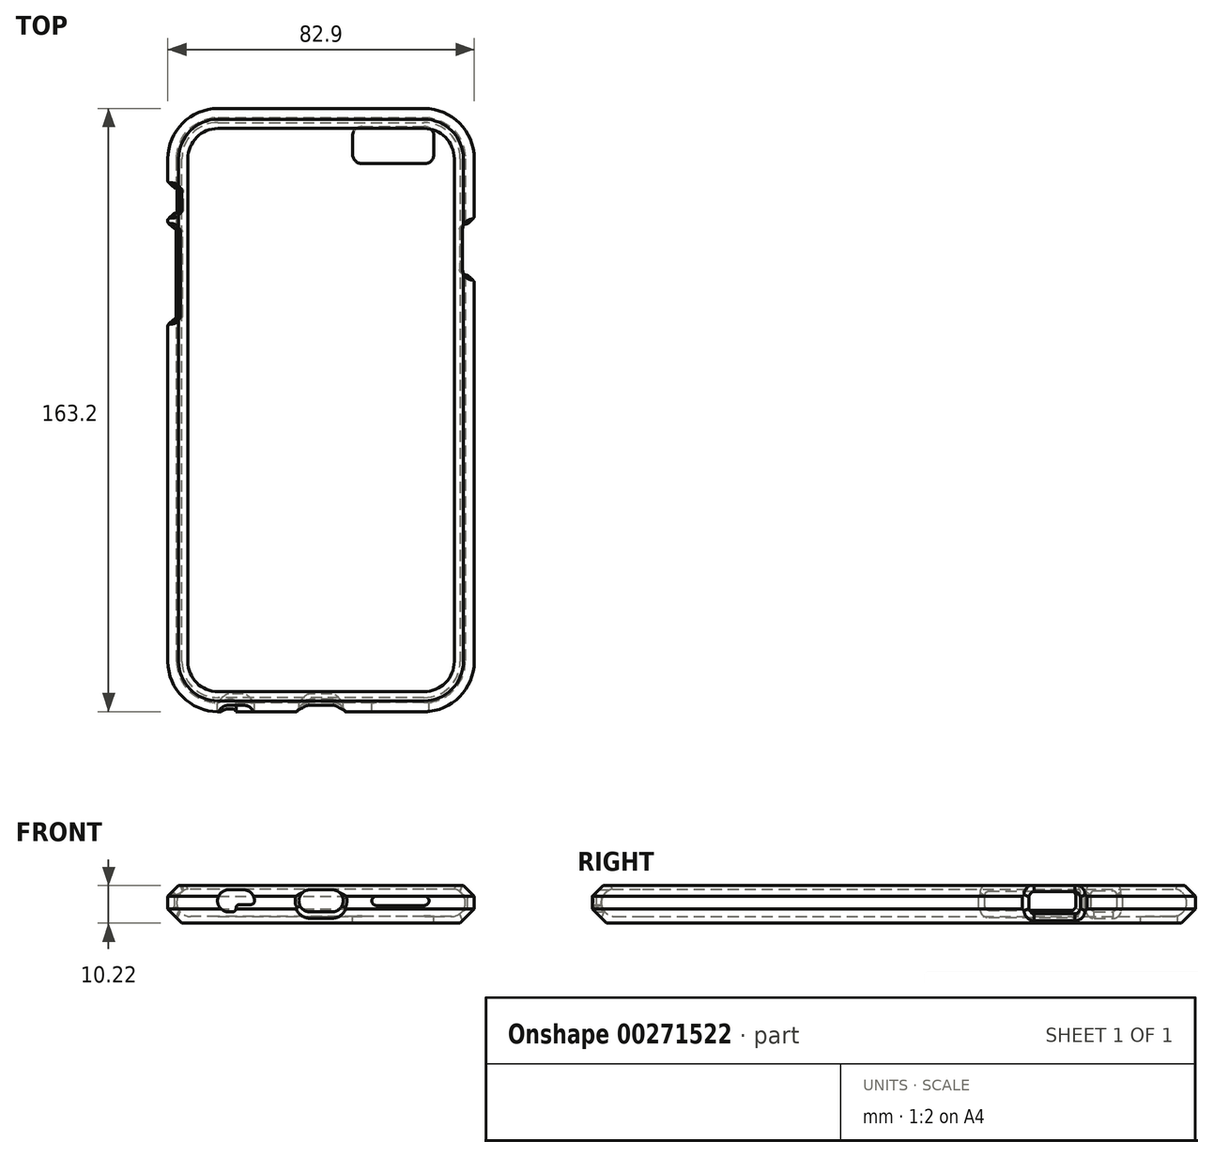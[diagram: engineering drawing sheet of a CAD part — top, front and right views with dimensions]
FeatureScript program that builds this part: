
annotation { "Feature Type Name" : "Feature", "Feature Type Description" : "" }
export const myFeature = defineFeature(function(context is Context, id is Id, definition is map)
    precondition{}
    {
        {
            assignVariable(context, id + "F0", {"name" : "HoleChamferLength", "anyValue" : 1.25});
        }
        {
            assignVariable(context, id + "F1", {"name" : "HoleChamferTopBottom", "anyValue" : 1.75});
        }
        {
            var Q0;
            Q0=qCreatedBy(makeId("Top.planeOp"),FACE);
            var sketch = newSketch(context, id + "F2", { "sketchPlane" : qUnion([Q0])});
            skLineSegment(sketch, "E0.bottom", {"start": v(27.85, 79.2) * mm, "end": v(0, 79.2) * mm});
            skLineSegment(sketch, "E0.top", {"start": v(27.85, -79.2) * mm, "end": v(-27.85, -79.2) * mm});
            skLineSegment(sketch, "E0.left", {"start": v(39.05, 68) * mm, "end": v(39.05, -68) * mm});
            skLineSegment(sketch, "E0.right", {"start": v(-39.05, 68) * mm, "end": v(-39.05, -68) * mm});
            skPoint(sketch, "E0.middle", {"position": v(0, 0) * mm});
            skPoint(sketch, "E1.visualSharp", {"position": v(-39.05, 79.2) * mm});
            skArc(sketch, "E1.filletArc", {"start": v(-27.85, 79.2) * mm, "mid": v(-35.77, 75.92) * mm, "end": v(-39.05, 68) * mm});
            skPoint(sketch, "E2.visualSharp", {"position": v(39.05, 79.2) * mm});
            skArc(sketch, "E2.filletArc", {"start": v(39.05, 68) * mm, "mid": v(35.77, 75.92) * mm, "end": v(27.85, 79.2) * mm});
            skPoint(sketch, "E3.visualSharp", {"position": v(39.05, -79.2) * mm});
            skArc(sketch, "E3.filletArc", {"start": v(27.85, -79.2) * mm, "mid": v(35.77, -75.92) * mm, "end": v(39.05, -68) * mm});
            skPoint(sketch, "E4.visualSharp", {"position": v(-39.05, -79.2) * mm});
            skArc(sketch, "E4.filletArc", {"start": v(-39.05, -68) * mm, "mid": v(-35.77, -75.92) * mm, "end": v(-27.85, -79.2) * mm});
            skLineSegment(sketch, "E5", {"start": v(0, 79.2) * mm, "end": v(-27.85, 79.2) * mm});
            skSolve(sketch);
        }
        {
            var Q0;
            Q0=qCreatedBy(makeId("Right.planeOp"),FACE);
            var sketch = newSketch(context, id + "F3", { "sketchPlane" : qUnion([Q0])});
            skPoint(sketch, "E6.0", {"position": v(79.2, 0) * mm});
            skArc(sketch, "E7", {"start": v(75.45, -3.75) * mm, "mid": v(79.2, 0) * mm, "end": v(75.45, 3.75) * mm});
            skLineSegment(sketch, "E8", {"start": v(75.45, -3.75) * mm, "end": v(75.45, 3.75) * mm, "construction": true});
            skLineSegment(sketch, "E9", {"start": v(81.6, -1.75) * mm, "end": v(81.6, 1.75) * mm});
            skLineSegment(sketch, "E10", {"start": v(81.6, 1.75) * mm, "end": v(79.85, 3.5) * mm});
            skLineSegment(sketch, "E11.trimOffspring", {"start": v(79.85, -3.5) * mm, "end": v(81.6, -1.75) * mm});
            skLineSegment(sketch, "E12", {"start": v(75.45, -5.55) * mm, "end": v(75.45, -3.75) * mm});
            skLineSegment(sketch, "E13", {"start": v(75.45, -5.55) * mm, "end": v(84.8, -5.55) * mm, "construction": true});
            skPoint(sketch, "E14", {"position": v(81.6, 0) * mm});
            skPoint(sketch, "E15.visualSharp", {"position": v(66.64, 4.7) * mm});
            skArc(sketch, "E15.filletArc", {"start": v(77.42, 4.67) * mm, "mid": v(76.63, 4.4) * mm, "end": v(76.2, 3.67) * mm});
            skLineSegment(sketch, "E16", {"start": v(79.85, -3.5) * mm, "end": v(77.8, -5.55) * mm});
            skLineSegment(sketch, "E17", {"start": v(77.8, -5.55) * mm, "end": v(75.45, -5.55) * mm});
            skLineSegment(sketch, "E18", {"start": v(79.85, 3.5) * mm, "end": v(78.68, 4.67) * mm});
            skLineSegment(sketch, "E19", {"start": v(78.68, 4.67) * mm, "end": v(77.42, 4.67) * mm});
            skLineSegment(sketch, "E20", {"start": v(76.2, 3.67) * mm, "end": v(66.74, 5.6) * mm, "construction": true});
            skSolve(sketch);
        }
        {
            var Q0;
            Q0=sQuery(id+"F2.wireOp",EDGE,"E5");
            var Q1;
            Q1=sQuery(id+"F2.wireOp",VERTEX,"E5.end");
            cPlane(context, id + "F4", {"entities" : qUnion([Q0, Q1]), "cplaneType" : CPlaneType.LINE_POINT, "offset" : 25 * mm, "width" : 150 * mm, "height" : 150 * mm});
        }
        {
            var Q0;
            Q0=sQuery(id+"F2.wireOp",EDGE,"E0.bottom");
            var Q1;
            Q1=sQuery(id+"F2.wireOp",VERTEX,"E2.filletArc.end");
            cPlane(context, id + "F5", {"entities" : qUnion([Q0, Q1]), "cplaneType" : CPlaneType.LINE_POINT, "offset" : 25 * mm, "width" : 150 * mm, "height" : 150 * mm});
        }
        {
            var Q0;
            Q0=sQuery(id+"F2.wireOp",EDGE,"E0.right");
            var Q1;
            Q1=sQuery(id+"F2.wireOp",VERTEX,"E0.right.end");
            cPlane(context, id + "F6", {"entities" : qUnion([Q0, Q1]), "cplaneType" : CPlaneType.LINE_POINT, "offset" : 25 * mm, "width" : 150 * mm, "height" : 150 * mm});
        }
        {
            var Q0;
            Q0=qCreatedBy(id+"F4.planeOp",FACE);
            var sketch = newSketch(context, id + "F7", { "sketchPlane" : qUnion([Q0])});
            skLineSegment(sketch, "E21.bottom", {"start": v(-25.55, -1.88) * mm, "end": v(-48.2, -1.88) * mm});
            skLineSegment(sketch, "E21.top", {"start": v(-25.55, 2.87) * mm, "end": v(-48.2, 2.87) * mm});
            skLineSegment(sketch, "E21.left", {"start": v(-24.55, -0.88) * mm, "end": v(-24.55, 1.87) * mm});
            skLineSegment(sketch, "E21.right", {"start": v(-49.2, -0.88) * mm, "end": v(-49.2, 1.87) * mm});
            skPoint(sketch, "E21.middle", {"position": v(-36.87, 0.5) * mm});
            skPoint(sketch, "E22.visualSharp", {"position": v(-49.2, 2.87) * mm});
            skArc(sketch, "E22.filletArc", {"start": v(-48.2, 2.87) * mm, "mid": v(-48.9, 2.58) * mm, "end": v(-49.2, 1.87) * mm});
            skPoint(sketch, "E23.visualSharp", {"position": v(-49.2, -1.88) * mm});
            skArc(sketch, "E23.filletArc", {"start": v(-49.2, -0.88) * mm, "mid": v(-48.9, -1.58) * mm, "end": v(-48.2, -1.88) * mm});
            skPoint(sketch, "E24.visualSharp", {"position": v(-24.55, 2.87) * mm});
            skArc(sketch, "E24.filletArc", {"start": v(-24.55, 1.87) * mm, "mid": v(-24.84, 2.58) * mm, "end": v(-25.55, 2.87) * mm});
            skPoint(sketch, "E25.visualSharp", {"position": v(-24.55, -1.88) * mm});
            skArc(sketch, "E25.filletArc", {"start": v(-25.55, -1.88) * mm, "mid": v(-24.84, -1.58) * mm, "end": v(-24.55, -0.88) * mm});
            skLineSegment(sketch, "E26.bottom", {"start": v(-59.2, 3.12) * mm, "end": v(-54.2, 3.12) * mm});
            skLineSegment(sketch, "E26.top", {"start": v(-59.2, -2.13) * mm, "end": v(-54.2, -2.13) * mm});
            skLineSegment(sketch, "E26.left", {"start": v(-60.2, 2.12) * mm, "end": v(-60.2, -1.13) * mm});
            skLineSegment(sketch, "E26.right", {"start": v(-53.2, 2.12) * mm, "end": v(-53.2, -1.13) * mm});
            skPoint(sketch, "E26.middle", {"position": v(-56.7, 0.5) * mm});
            skPoint(sketch, "E27.visualSharp", {"position": v(-60.2, 3.12) * mm});
            skArc(sketch, "E27.filletArc", {"start": v(-59.2, 3.12) * mm, "mid": v(-59.9, 2.83) * mm, "end": v(-60.2, 2.12) * mm});
            skPoint(sketch, "E28.visualSharp", {"position": v(-60.2, -2.13) * mm});
            skArc(sketch, "E28.filletArc", {"start": v(-60.2, -1.13) * mm, "mid": v(-59.9, -1.83) * mm, "end": v(-59.2, -2.13) * mm});
            skPoint(sketch, "E29.visualSharp", {"position": v(-53.2, -2.13) * mm});
            skArc(sketch, "E29.filletArc", {"start": v(-54.2, -2.13) * mm, "mid": v(-53.5, -1.83) * mm, "end": v(-53.2, -1.13) * mm});
            skPoint(sketch, "E30.visualSharp", {"position": v(-53.2, 3.12) * mm});
            skArc(sketch, "E30.filletArc", {"start": v(-53.2, 2.12) * mm, "mid": v(-53.5, 2.83) * mm, "end": v(-54.2, 3.12) * mm});
            skSolve(sketch);
        }
        {
            var Q0;
            Q0=qCreatedBy(id+"F5.planeOp",FACE);
            var sketch = newSketch(context, id + "F8", { "sketchPlane" : qUnion([Q0])});
            skLineSegment(sketch, "E31.bottom", {"start": v(-48.95, 2.75) * mm, "end": v(-37.95, 2.75) * mm});
            skLineSegment(sketch, "E31.top", {"start": v(-48.95, -2.75) * mm, "end": v(-37.95, -2.75) * mm});
            skLineSegment(sketch, "E31.left", {"start": v(-50.45, 1.25) * mm, "end": v(-50.45, -1.25) * mm});
            skLineSegment(sketch, "E31.right", {"start": v(-36.45, 1.25) * mm, "end": v(-36.45, -1.25) * mm});
            skPoint(sketch, "E31.middle", {"position": v(-43.45, 0) * mm});
            skPoint(sketch, "E32.visualSharp", {"position": v(-50.45, 2.75) * mm});
            skArc(sketch, "E32.filletArc", {"start": v(-48.95, 2.75) * mm, "mid": v(-50.01, 2.31) * mm, "end": v(-50.45, 1.25) * mm});
            skPoint(sketch, "E33.visualSharp", {"position": v(-50.45, -2.75) * mm});
            skArc(sketch, "E33.filletArc", {"start": v(-50.45, -1.25) * mm, "mid": v(-50.01, -2.31) * mm, "end": v(-48.95, -2.75) * mm});
            skPoint(sketch, "E34.visualSharp", {"position": v(-36.45, -2.75) * mm});
            skArc(sketch, "E34.filletArc", {"start": v(-37.95, -2.75) * mm, "mid": v(-36.89, -2.31) * mm, "end": v(-36.45, -1.25) * mm});
            skPoint(sketch, "E35.visualSharp", {"position": v(-36.45, 2.75) * mm});
            skArc(sketch, "E35.filletArc", {"start": v(-36.45, 1.25) * mm, "mid": v(-36.89, 2.31) * mm, "end": v(-37.95, 2.75) * mm});
            skSolve(sketch);
        }
        {
            var Q0;
            Q0=qCreatedBy(id+"F6.planeOp",FACE);
            var sketch = newSketch(context, id + "F9", { "sketchPlane" : qUnion([Q0])});
            skLineSegment(sketch, "E36.bottom", {"start": v(3, 3.5) * mm, "end": v(-3, 3.5) * mm});
            skLineSegment(sketch, "E36.top", {"start": v(3, -2.5) * mm, "end": v(-3, -2.5) * mm});
            skLineSegment(sketch, "E36.left", {"start": v(6, 0.5) * mm, "end": v(6, 0.5) * mm});
            skLineSegment(sketch, "E36.right", {"start": v(-6, 0.5) * mm, "end": v(-6, 0.5) * mm});
            skPoint(sketch, "E36.middle", {"position": v(0, 0.5) * mm});
            skArc(sketch, "E37", {"start": v(-25, 3.5) * mm, "mid": v(-28, 0.5) * mm, "end": v(-25, -2.5) * mm});
            skPoint(sketch, "E38.visualSharp", {"position": v(-6, 3.5) * mm});
            skArc(sketch, "E38.filletArc", {"start": v(-3, 3.5) * mm, "mid": v(-5.12, 2.62) * mm, "end": v(-6, 0.5) * mm});
            skPoint(sketch, "E39.visualSharp", {"position": v(-6, -2.5) * mm});
            skArc(sketch, "E39.filletArc", {"start": v(-6, 0.5) * mm, "mid": v(-5.12, -1.62) * mm, "end": v(-3, -2.5) * mm});
            skPoint(sketch, "E40.visualSharp", {"position": v(6, -2.5) * mm});
            skArc(sketch, "E40.filletArc", {"start": v(3, -2.5) * mm, "mid": v(5.12, -1.62) * mm, "end": v(6, 0.5) * mm});
            skPoint(sketch, "E41.visualSharp", {"position": v(6, 3.5) * mm});
            skArc(sketch, "E41.filletArc", {"start": v(6, 0.5) * mm, "mid": v(5.12, 2.62) * mm, "end": v(3, 3.5) * mm});
            skArc(sketch, "E42", {"start": v(-21, -2.5) * mm, "mid": v(-19.27, -1.95) * mm, "end": v(-18.17, -0.5) * mm, "construction": true});
            skLineSegment(sketch, "E43", {"start": v(-21, 3.5) * mm, "end": v(-25, 3.5) * mm});
            skLineSegment(sketch, "E44", {"start": v(-21, -2.5) * mm, "end": v(-23, -2.5) * mm, "construction": true});
            skLineSegment(sketch, "E45", {"start": v(15, 0.5) * mm, "end": v(28, 0.5) * mm, "construction": true});
            skArc(sketch, "E46.0.startCap", {"start": v(15, -0.75) * mm, "mid": v(13.75, 0.5) * mm, "end": v(15, 1.75) * mm});
            skArc(sketch, "E46.0.endCap", {"start": v(28, 1.75) * mm, "mid": v(29.25, 0.5) * mm, "end": v(28, -0.75) * mm});
            skLineSegment(sketch, "E46.0.left", {"start": v(15, 1.75) * mm, "end": v(28, 1.75) * mm});
            skLineSegment(sketch, "E46.0.right", {"start": v(15, -0.75) * mm, "end": v(28, -0.75) * mm});
            skLineSegment(sketch, "E47", {"start": v(-23, -1.5) * mm, "end": v(-23, -1.5) * mm});
            skLineSegment(sketch, "E48", {"start": v(-22, -0.5) * mm, "end": v(-19, -0.5) * mm});
            skLineSegment(sketch, "E49", {"start": v(-24, -2.5) * mm, "end": v(-25, -2.5) * mm});
            skArc(sketch, "E50", {"start": v(-18, 0.5) * mm, "mid": v(-18.88, 2.62) * mm, "end": v(-21, 3.5) * mm});
            skPoint(sketch, "E51.visualSharp", {"position": v(-23, -0.5) * mm});
            skArc(sketch, "E51.filletArc", {"start": v(-22, -0.5) * mm, "mid": v(-22.7, -0.8) * mm, "end": v(-23, -1.5) * mm});
            skPoint(sketch, "E52.visualSharp", {"position": v(-23, -2.5) * mm});
            skArc(sketch, "E52.filletArc", {"start": v(-24, -2.5) * mm, "mid": v(-23.3, -2.2) * mm, "end": v(-23, -1.5) * mm});
            skPoint(sketch, "E53.visualSharp", {"position": v(-18.17, -0.5) * mm});
            skArc(sketch, "E53.filletArc", {"start": v(-19, -0.5) * mm, "mid": v(-18.3, -0.2) * mm, "end": v(-18, 0.5) * mm});
            skCircle(sketch, "E54", {"center": v(-25, 0.5) * mm, "radius": 2.5 * mm, "construction": true});
            skSolve(sketch);
        }
        {
            var Q0;
            Q0=qCreatedBy(makeId("Top.planeOp"),FACE);
            var sketch = newSketch(context, id + "F10", { "sketchPlane" : qUnion([Q0])});
            skLineSegment(sketch, "E55.bottom", {"start": v(28.05, 66.7) * mm, "end": v(11.05, 66.7) * mm});
            skLineSegment(sketch, "E55.top", {"start": v(28.05, 76.7) * mm, "end": v(11.05, 76.7) * mm});
            skLineSegment(sketch, "E55.left", {"start": v(30.55, 69.2) * mm, "end": v(30.55, 74.2) * mm});
            skLineSegment(sketch, "E55.right", {"start": v(8.55, 69.2) * mm, "end": v(8.55, 74.2) * mm});
            skPoint(sketch, "E55.middle", {"position": v(19.55, 71.7) * mm});
            skPoint(sketch, "E56.visualSharp", {"position": v(8.55, 76.7) * mm});
            skArc(sketch, "E56.filletArc", {"start": v(11.05, 76.7) * mm, "mid": v(9.28, 75.97) * mm, "end": v(8.55, 74.2) * mm});
            skPoint(sketch, "E57.visualSharp", {"position": v(8.55, 66.7) * mm});
            skArc(sketch, "E57.filletArc", {"start": v(8.55, 69.2) * mm, "mid": v(9.28, 67.43) * mm, "end": v(11.05, 66.7) * mm});
            skPoint(sketch, "E58.visualSharp", {"position": v(30.55, 66.7) * mm});
            skArc(sketch, "E58.filletArc", {"start": v(28.05, 66.7) * mm, "mid": v(29.82, 67.43) * mm, "end": v(30.55, 69.2) * mm});
            skPoint(sketch, "E59.visualSharp", {"position": v(30.55, 76.7) * mm});
            skArc(sketch, "E59.filletArc", {"start": v(30.55, 74.2) * mm, "mid": v(29.82, 75.97) * mm, "end": v(28.05, 76.7) * mm});
            skSolve(sketch);
        }
        {
            var Q0;
            Q0=qSketchRegion(id+"F3",true);
            var Q1;
            Q1=sQuery(id+"F2.wireOp",EDGE,"E5");
            var Q2;
            Q2=sQuery(id+"F2.wireOp",EDGE,"E1.filletArc");
            var Q3;
            Q3=sQuery(id+"F2.wireOp",EDGE,"E0.right");
            var Q4;
            Q4=sQuery(id+"F2.wireOp",EDGE,"E4.filletArc");
            var Q5;
            Q5=sQuery(id+"F2.wireOp",EDGE,"E0.top");
            var Q6;
            Q6=sQuery(id+"F2.wireOp",EDGE,"E3.filletArc");
            var Q7;
            Q7=sQuery(id+"F2.wireOp",EDGE,"E0.left");
            var Q8;
            Q8=sQuery(id+"F2.wireOp",EDGE,"E2.filletArc");
            var Q9;
            Q9=sQuery(id+"F2.wireOp",EDGE,"E0.bottom");
            sweep(context, id + "F11", {"profiles" : qUnion([Q0]), "path" : qUnion([Q1, Q2, Q3, Q4, Q5, Q6, Q7, Q8, Q9])});
        }
        {
            var Q0;
            Q0=qCreatedBy(makeId("Front.planeOp"),FACE);
            var sketch = newSketch(context, id + "F12", { "sketchPlane" : qUnion([Q0])});
            skLineSegment(sketch, "E60.0.0", {"start": v(35.3, -5.55) * mm, "end": v(27.85, -5.55) * mm});
            skLineSegment(sketch, "E60.0.1", {"start": v(27.85, -3.75) * mm, "end": v(27.85, -5.55) * mm});
            skLineSegment(sketch, "E60.0.2", {"start": v(27.85, -3.75) * mm, "end": v(35.3, -3.75) * mm});
            skLineSegment(sketch, "E60.0.3", {"start": v(35.3, -3.75) * mm, "end": v(35.3, -5.55) * mm});
            skLineSegment(sketch, "E60.1.0", {"start": v(27.85, -5.55) * mm, "end": v(-27.85, -5.55) * mm});
            skLineSegment(sketch, "E60.1.1", {"start": v(-27.85, -3.75) * mm, "end": v(-27.85, -5.55) * mm});
            skLineSegment(sketch, "E60.1.2", {"start": v(-27.85, -3.75) * mm, "end": v(27.85, -3.75) * mm});
            skLineSegment(sketch, "E60.1.3", {"start": v(27.85, -3.75) * mm, "end": v(27.85, -5.55) * mm});
            skLineSegment(sketch, "E60.2.0", {"start": v(-27.85, -5.55) * mm, "end": v(-35.3, -5.55) * mm});
            skLineSegment(sketch, "E60.2.1", {"start": v(-35.3, -3.75) * mm, "end": v(-35.3, -5.55) * mm});
            skLineSegment(sketch, "E60.2.2", {"start": v(-35.3, -3.75) * mm, "end": v(-27.85, -3.75) * mm});
            skLineSegment(sketch, "E60.2.3", {"start": v(-27.85, -3.75) * mm, "end": v(-27.85, -5.55) * mm});
            skSolve(sketch);
        }
        {
            var Q0;
            Q0=qSketchRegion(id+"F12",true);
            extrude(context, id + "F13", {"entities" : qUnion([Q0]), "operationType" : NewBodyOperationType.ADD, "endBound" : BoundingType.UP_TO_NEXT, "depth" : 25 * mm, "hasSecondDirection" : true, "secondDirectionBound" : SecondDirectionBoundingType.UP_TO_NEXT, "secondDirectionOppositeDirection" : true, "secondDirectionDepth" : 25 * mm});
        }
        {
            var Q0;
            Q0=qSketchRegion(id+"F7",true);
            extrude(context, id + "F14", {"entities" : qUnion([Q0]), "operationType" : NewBodyOperationType.REMOVE, "endBound" : BoundingType.THROUGH_ALL, "depth" : 25 * mm});
        }
        {
            var Q0;
            Q0=qSketchRegion(id+"F8",true);
            extrude(context, id + "F15", {"entities" : qUnion([Q0]), "operationType" : NewBodyOperationType.REMOVE, "endBound" : BoundingType.THROUGH_ALL, "oppositeDirection" : true, "depth" : 25 * mm});
        }
        {
            var Q0;
            Q0=makeQuery(id+"F10.imprint","IMPRINT",FACE,{"disambiguationData":[TD([[makeQuery(id+"F10.imprint","IMPRINT",EDGE,{"derivedFrom":sQuery(id+"F10.wireOp",EDGE,"E55.bottom")}),-1.0]])]});
            extrude(context, id + "F16", {"entities" : qUnion([Q0]), "operationType" : NewBodyOperationType.REMOVE, "endBound" : BoundingType.THROUGH_ALL, "oppositeDirection" : true, "depth" : 25 * mm});
        }
        {
            var Q0;
            Q0=qSketchRegion(id+"F9",true);
            extrude(context, id + "F17", {"entities" : qUnion([Q0]), "operationType" : NewBodyOperationType.REMOVE, "endBound" : BoundingType.THROUGH_ALL, "depth" : 25 * mm});
        }
        {
            var Q0;
            Q0=makeQuery(id+"F14.boolean.opBoolean","INTERSECT",EDGE,{"derivedFrom":[makeQuery(id+"F11.opSweep","SWEPT_FACE",FACE,{"disambiguationData":[OSD([sQuery(id+"F2.wireOp",EDGE,"E0.right"),sQuery(id+"F3.wireOp",EDGE,"E11.trimOffspring"),sQuery(id+"F3.wireOp",EDGE,"E16")])]}),makeQuery(id+"F14.opExtrude","SWEPT_FACE",FACE,{"disambiguationData":[OSD([sQuery(id+"F7.wireOp",EDGE,"E21.bottom")])]})]});
            var Q1;
            Q1=makeQuery(id+"F14.boolean.opBoolean","INTERSECT",EDGE,{"derivedFrom":[makeQuery(id+"F11.opSweep","SWEPT_FACE",FACE,{"disambiguationData":[OSD([sQuery(id+"F2.wireOp",EDGE,"E0.right"),sQuery(id+"F3.wireOp",EDGE,"E10")])]}),makeQuery(id+"F14.opExtrude","SWEPT_FACE",FACE,{"disambiguationData":[OSD([sQuery(id+"F7.wireOp",EDGE,"E21.top")])]})]});
            chamfer(context, id + "F18", {"entities" : qUnion([Q0, Q1]), "width" : (getVariable(context, 'HoleChamferLength')) * mm, "tangentPropagation" : true});
        }
        {
            var Q0;
            Q0=makeQuery(id+"F14.boolean.opBoolean","INTERSECT",EDGE,{"derivedFrom":[makeQuery(id+"F11.opSweep","SWEPT_FACE",FACE,{"disambiguationData":[OSD([sQuery(id+"F2.wireOp",EDGE,"E0.right"),sQuery(id+"F3.wireOp",EDGE,"E11.trimOffspring"),sQuery(id+"F3.wireOp",EDGE,"E16")])]}),makeQuery(id+"F14.opExtrude","SWEPT_FACE",FACE,{"disambiguationData":[OSD([sQuery(id+"F7.wireOp",EDGE,"E26.top")])]})]});
            var Q1;
            Q1=makeQuery(id+"F14.boolean.opBoolean","INTERSECT",EDGE,{"derivedFrom":[makeQuery(id+"F11.opSweep","SWEPT_FACE",FACE,{"disambiguationData":[OSD([sQuery(id+"F2.wireOp",EDGE,"E0.right"),sQuery(id+"F3.wireOp",EDGE,"E10")])]}),makeQuery(id+"F14.opExtrude","SWEPT_FACE",FACE,{"disambiguationData":[OSD([sQuery(id+"F7.wireOp",EDGE,"E26.bottom")])]})]});
            chamfer(context, id + "F19", {"entities" : qUnion([Q0, Q1]), "width" : (getVariable(context, 'HoleChamferLength')) * mm, "tangentPropagation" : true});
        }
        {
            var Q0;
            Q0=makeQuery(id+"F15.boolean.opBoolean","INTERSECT",EDGE,{"derivedFrom":[makeQuery(id+"F11.opSweep","SWEPT_FACE",FACE,{"disambiguationData":[OSD([sQuery(id+"F2.wireOp",EDGE,"E0.left"),sQuery(id+"F3.wireOp",EDGE,"E11.trimOffspring"),sQuery(id+"F3.wireOp",EDGE,"E16")])]}),makeQuery(id+"F15.opExtrude","SWEPT_FACE",FACE,{"disambiguationData":[OSD([sQuery(id+"F8.wireOp",EDGE,"E31.top")])]})]});
            var Q1;
            Q1=makeQuery(id+"F15.boolean.opBoolean","INTERSECT",EDGE,{"derivedFrom":[makeQuery(id+"F11.opSweep","SWEPT_FACE",FACE,{"disambiguationData":[OSD([sQuery(id+"F2.wireOp",EDGE,"E0.left"),sQuery(id+"F3.wireOp",EDGE,"E10")])]}),makeQuery(id+"F15.opExtrude","SWEPT_FACE",FACE,{"disambiguationData":[OSD([sQuery(id+"F8.wireOp",EDGE,"E31.bottom")])]})]});
            chamfer(context, id + "F20", {"entities" : qUnion([Q0, Q1]), "width" : (getVariable(context, 'HoleChamferLength')) * mm, "tangentPropagation" : true});
        }
        {
            var Q0;
            Q0=makeQuery(id+"F15.boolean.opBoolean","INTERSECT",EDGE,{"derivedFrom":[makeQuery(id+"F11.opSweep","SWEPT_FACE",FACE,{"disambiguationData":[OSD([sQuery(id+"F2.wireOp",EDGE,"E0.left"),sQuery(id+"F3.wireOp",EDGE,"E9")])]}),makeQuery(id+"F15.opExtrude","SWEPT_FACE",FACE,{"disambiguationData":[OSD([sQuery(id+"F8.wireOp",EDGE,"E31.left")])]})]});
            var Q1;
            Q1=makeQuery(id+"F15.boolean.opBoolean","INTERSECT",EDGE,{"derivedFrom":[makeQuery(id+"F11.opSweep","SWEPT_FACE",FACE,{"disambiguationData":[OSD([sQuery(id+"F2.wireOp",EDGE,"E0.left"),sQuery(id+"F3.wireOp",EDGE,"E9")])]}),makeQuery(id+"F15.opExtrude","SWEPT_FACE",FACE,{"disambiguationData":[OSD([sQuery(id+"F8.wireOp",EDGE,"E31.right")])]})]});
            var Q2;
            Q2=makeQuery(id+"F14.boolean.opBoolean","INTERSECT",EDGE,{"derivedFrom":[makeQuery(id+"F11.opSweep","SWEPT_FACE",FACE,{"disambiguationData":[OSD([sQuery(id+"F2.wireOp",EDGE,"E0.right"),sQuery(id+"F3.wireOp",EDGE,"E9")])]}),makeQuery(id+"F14.opExtrude","SWEPT_FACE",FACE,{"disambiguationData":[OSD([sQuery(id+"F7.wireOp",EDGE,"E21.left")])]})]});
            var Q3;
            Q3=makeQuery(id+"F14.boolean.opBoolean","INTERSECT",EDGE,{"derivedFrom":[makeQuery(id+"F11.opSweep","SWEPT_FACE",FACE,{"disambiguationData":[OSD([sQuery(id+"F2.wireOp",EDGE,"E0.right"),sQuery(id+"F3.wireOp",EDGE,"E9")])]}),makeQuery(id+"F14.opExtrude","SWEPT_FACE",FACE,{"disambiguationData":[OSD([sQuery(id+"F7.wireOp",EDGE,"E21.right")])]})]});
            var Q4;
            Q4=makeQuery(id+"F14.boolean.opBoolean","INTERSECT",EDGE,{"derivedFrom":[makeQuery(id+"F11.opSweep","SWEPT_FACE",FACE,{"disambiguationData":[OSD([sQuery(id+"F2.wireOp",EDGE,"E0.right"),sQuery(id+"F3.wireOp",EDGE,"E9")])]}),makeQuery(id+"F14.opExtrude","SWEPT_FACE",FACE,{"disambiguationData":[OSD([sQuery(id+"F7.wireOp",EDGE,"E26.left")])]})]});
            var Q5;
            Q5=makeQuery(id+"F14.boolean.opBoolean","INTERSECT",EDGE,{"derivedFrom":[makeQuery(id+"F11.opSweep","SWEPT_FACE",FACE,{"disambiguationData":[OSD([sQuery(id+"F2.wireOp",EDGE,"E0.right"),sQuery(id+"F3.wireOp",EDGE,"E9")])]}),makeQuery(id+"F14.opExtrude","SWEPT_FACE",FACE,{"disambiguationData":[OSD([sQuery(id+"F7.wireOp",EDGE,"E26.right")])]})]});
            chamfer(context, id + "F21", {"entities" : qUnion([Q0, Q1, Q2, Q3, Q4, Q5]), "width" : (getVariable(context, 'HoleChamferTopBottom')) * mm, "tangentPropagation" : true});
        }
        {
            var Q0;
            Q0=makeQuery(id+"F17.boolean.opBoolean","INTERSECT",EDGE,{"derivedFrom":[makeQuery(id+"F11.opSweep","SWEPT_FACE",FACE,{"disambiguationData":[OSD([sQuery(id+"F2.wireOp",EDGE,"E0.top"),sQuery(id+"F3.wireOp",EDGE,"E11.trimOffspring"),sQuery(id+"F3.wireOp",EDGE,"E16")])]}),makeQuery(id+"F17.opExtrude","SWEPT_FACE",FACE,{"disambiguationData":[OSD([sQuery(id+"F9.wireOp",EDGE,"E36.top")])]})]});
            var Q1;
            Q1=makeQuery(id+"F17.boolean.opBoolean","INTERSECT",EDGE,{"derivedFrom":[makeQuery(id+"F11.opSweep","SWEPT_FACE",FACE,{"disambiguationData":[OSD([sQuery(id+"F2.wireOp",EDGE,"E0.top"),sQuery(id+"F3.wireOp",EDGE,"E9")])]}),makeQuery(id+"F17.opExtrude","SWEPT_FACE",FACE,{"disambiguationData":[OSD([sQuery(id+"F9.wireOp",EDGE,"E38.filletArc"),sQuery(id+"F9.wireOp",EDGE,"E39.filletArc")])]})]});
            var Q2;
            Q2=makeQuery(id+"F17.boolean.opBoolean","INTERSECT",EDGE,{"derivedFrom":[makeQuery(id+"F11.opSweep","SWEPT_FACE",FACE,{"disambiguationData":[OSD([sQuery(id+"F2.wireOp",EDGE,"E0.top"),sQuery(id+"F3.wireOp",EDGE,"E9")])]}),makeQuery(id+"F17.opExtrude","SWEPT_FACE",FACE,{"disambiguationData":[OSD([sQuery(id+"F9.wireOp",EDGE,"E40.filletArc"),sQuery(id+"F9.wireOp",EDGE,"E41.filletArc")])]})]});
            chamfer(context, id + "F22", {"entities" : qUnion([Q0, Q1, Q2]), "width" : 1 * mm, "tangentPropagation" : true});
        }
    });
